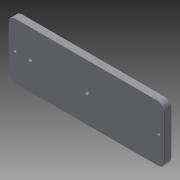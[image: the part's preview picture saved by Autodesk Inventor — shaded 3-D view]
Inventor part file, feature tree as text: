
AUTODESK INVENTOR PART (.ipt)
format: ipt  version: 2015 (Build 190159000, 159)  size: 122,368 bytes
history: native  units: in
note: dims shown in document units (in); Inventor stores cm internally (conversion verified against a paired STEP export)
features: hole x4, sketch x2, extrude x1, chamfer x1
ambient origin geometry x8: Origin, YZ Plane, XZ Plane, XY Plane, X Axis, Y Axis, Z Axis, Center Point
bodies: Solid1 (feature_tree)
feature tree (8):
  sketch  "Sketch1"  dims[d0=11.0in d1=4.0in]
  extrude  "Extrusion1"  Depth=4.0in
  chamfer  "Chamfer1"  Distance=0.5in
  hole  "Hole5"  [1 undecoded]
  hole  "Hole6"  [1 undecoded]
  hole  "Hole7"  [1 undecoded]
  hole  "Hole8"  [1 undecoded]
  sketch  "Sketch2"  dims[d3=0.5in d8=0.5in d9=0.0in d17=0.0312in d18=0.125in d19=45.0deg d41=0.4375in d42=0.4375in d43=0.25in d44=0.75in d45=0.5in d46=0.25in d47=0.5635in d48=1.0in d49=0.8108in d50=0.25in d51=0.75in d52=0.5in d53=0.25in d54=0.5635in d55=1.0in d56=0.8108in d57=0.3125in d58=0.75in d59=0.5in d60=0.25in d61=0.5635in d62=1.0in d63=0.8108in d64=0.13in d65=0.287in d66=0.375in d67=0.25in d68=0.5635in d69=0.2875in d70=0.8108in]
note: 4 required parameter values undecoded (feature->parameter linkage not recoverable at this tier; creation-order binding heuristic only, values carry confidence <= 0.55)
